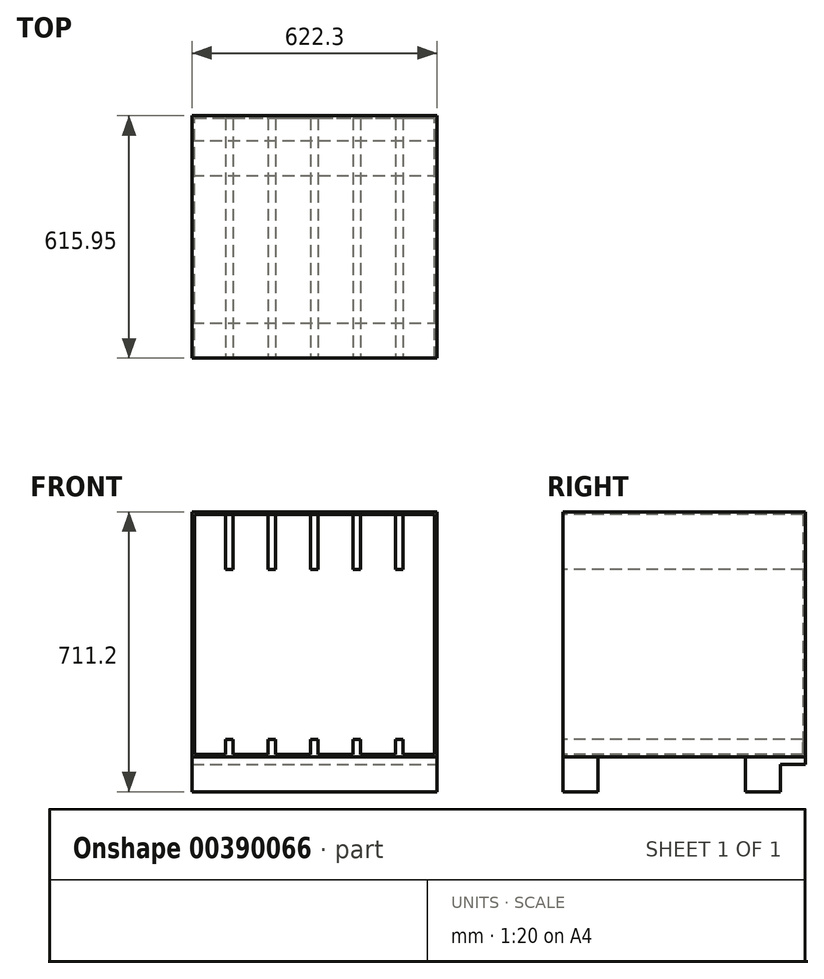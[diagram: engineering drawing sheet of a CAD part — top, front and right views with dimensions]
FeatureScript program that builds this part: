
annotation { "Feature Type Name" : "Feature", "Feature Type Description" : "" }
export const myFeature = defineFeature(function(context is Context, id is Id, definition is map)
    precondition{}
    {
        {
            var Q0;
            Q0=qCreatedBy(makeId("Front.planeOp"),FACE);
            var sketch = newSketch(context, id + "F0", { "sketchPlane" : qUnion([Q0])});
            skLineSegment(sketch, "E0.bottom", {"start": v(-311.15, 311.15) * mm, "end": v(311.15, 311.15) * mm});
            skLineSegment(sketch, "E0.top", {"start": v(-311.15, -311.15) * mm, "end": v(311.15, -311.15) * mm});
            skLineSegment(sketch, "E0.left", {"start": v(-311.15, 311.15) * mm, "end": v(-311.15, -311.15) * mm});
            skLineSegment(sketch, "E0.right", {"start": v(311.15, 311.15) * mm, "end": v(311.15, -311.15) * mm});
            skLineSegment(sketch, "E1", {"start": v(-311.15, 311.15) * mm, "end": v(311.15, -311.15) * mm, "construction": true});
            skSolve(sketch);
        }
        {
            var Q0;
            Q0 = qSketchRegion(id + "F0", true);
            extrude(context, id + "F1", {"entities" : qUnion([Q0]), "depth" : 615.95 * mm, "offsetDistance" : 25.4 * mm});
        }
        {
            var Q0;
            Q0=makeQuery(id+"F1.opExtrude","CAP_FACE",FACE,{"disambiguationData":[OSD([sQuery(id+"F0.wireOp",EDGE,"E0.bottom"),sQuery(id+"F0.wireOp",EDGE,"E0.top"),sQuery(id+"F0.wireOp",EDGE,"E0.left"),sQuery(id+"F0.wireOp",EDGE,"E0.right")])],"isStart":false});
            shell(context, id + "F2", {"entities" : qUnion([Q0]), "thickness" : 6.35 * mm});
        }
        {
            var Q0;
            Q0=makeQuery(id+"F1.opExtrude","SWEPT_FACE",FACE,{"disambiguationData":[OSD([sQuery(id+"F0.wireOp",EDGE,"E0.right")])]});
            var sketch = newSketch(context, id + "F3", { "sketchPlane" : qUnion([Q0])});
            skLineSegment(sketch, "E2.bottom", {"start": v(-615.95, -311.15) * mm, "end": v(-527.05, -311.15) * mm});
            skLineSegment(sketch, "E2.top", {"start": v(-615.95, -400.05) * mm, "end": v(-527.05, -400.05) * mm});
            skLineSegment(sketch, "E2.left", {"start": v(-615.95, -311.15) * mm, "end": v(-615.95, -400.05) * mm});
            skLineSegment(sketch, "E2.right", {"start": v(-527.05, -311.15) * mm, "end": v(-527.05, -400.05) * mm});
            skLineSegment(sketch, "E3.bottom", {"start": v(-63.5, -311.15) * mm, "end": v(-152.4, -311.15) * mm});
            skLineSegment(sketch, "E3.top", {"start": v(-63.5, -400.05) * mm, "end": v(-152.4, -400.05) * mm});
            skLineSegment(sketch, "E3.left", {"start": v(-63.5, -311.15) * mm, "end": v(-63.5, -400.05) * mm});
            skLineSegment(sketch, "E3.right", {"start": v(-152.4, -311.15) * mm, "end": v(-152.4, -400.05) * mm});
            skLineSegment(sketch, "E4.bottom", {"start": v(0, -311.15) * mm, "end": v(-63.5, -311.15) * mm});
            skLineSegment(sketch, "E4.top", {"start": v(0, -330.2) * mm, "end": v(-63.5, -330.2) * mm});
            skLineSegment(sketch, "E4.left", {"start": v(0, -311.15) * mm, "end": v(0, -330.2) * mm});
            skLineSegment(sketch, "E4.right", {"start": v(-63.5, -311.15) * mm, "end": v(-63.5, -330.2) * mm});
            skSolve(sketch);
        }
        {
            var Q0;
            Q0=makeQuery(id+"F3.imprint","IMPRINT",FACE,{"disambiguationData":[TD([[makeQuery(id+"F3.imprint","IMPRINT",EDGE,{"derivedFrom":sQuery(id+"F3.wireOp",EDGE,"E2.bottom")}),-1.0]])]});
            var Q1;
            Q1=makeQuery(id+"F3.imprint","IMPRINT",FACE,{"disambiguationData":[TD([[makeQuery(id+"F3.imprint","IMPRINT",EDGE,{"derivedFrom":sQuery(id+"F3.wireOp",EDGE,"E3.bottom")}),-1.0]])]});
            var Q2;
            Q2=makeQuery(id+"F3.imprint","IMPRINT",FACE,{"disambiguationData":[TD([[makeQuery(id+"F3.imprint","IMPRINT",EDGE,{"derivedFrom":sQuery(id+"F3.wireOp",EDGE,"E4.bottom")}),-1.0]])]});
            extrude(context, id + "F4", {"entities" : qUnion([Q0, Q1, Q2]), "oppositeDirection" : true, "depth" : 622.3 * mm, "offsetDistance" : 25.4 * mm});
        }
        {
            var Q0;
            Q0=makeQuery(id+"F1.opExtrude","CAP_FACE",FACE,{"disambiguationData":[OSD([sQuery(id+"F0.wireOp",EDGE,"E0.bottom"),sQuery(id+"F0.wireOp",EDGE,"E0.top"),sQuery(id+"F0.wireOp",EDGE,"E0.left"),sQuery(id+"F0.wireOp",EDGE,"E0.right")])],"isStart":false});
            var sketch = newSketch(context, id + "F5", { "sketchPlane" : qUnion([Q0])});
            skLineSegment(sketch, "E5.bottom", {"start": v(-225.43, -304.8) * mm, "end": v(-206.38, -304.8) * mm});
            skLineSegment(sketch, "E5.top", {"start": v(-225.43, -266.7) * mm, "end": v(-206.38, -266.7) * mm});
            skLineSegment(sketch, "E5.left", {"start": v(-225.43, -304.8) * mm, "end": v(-225.43, -266.7) * mm});
            skLineSegment(sketch, "E5.right", {"start": v(-206.38, -304.8) * mm, "end": v(-206.38, -266.7) * mm});
            skLineSegment(sketch, "E6.1.0.0", {"start": v(-117.48, -304.8) * mm, "end": v(-98.43, -304.8) * mm});
            skLineSegment(sketch, "E6.1.0.1", {"start": v(-98.43, -304.8) * mm, "end": v(-98.43, -266.7) * mm});
            skLineSegment(sketch, "E6.1.0.2", {"start": v(-117.48, -266.7) * mm, "end": v(-98.43, -266.7) * mm});
            skLineSegment(sketch, "E6.1.0.3", {"start": v(-117.48, -304.8) * mm, "end": v(-117.48, -266.7) * mm});
            skLineSegment(sketch, "E6.2.0.0", {"start": v(-9.53, -304.8) * mm, "end": v(9.52, -304.8) * mm});
            skLineSegment(sketch, "E6.2.0.1", {"start": v(9.52, -304.8) * mm, "end": v(9.52, -266.7) * mm});
            skLineSegment(sketch, "E6.2.0.2", {"start": v(-9.53, -266.7) * mm, "end": v(9.52, -266.7) * mm});
            skLineSegment(sketch, "E6.2.0.3", {"start": v(-9.53, -304.8) * mm, "end": v(-9.53, -266.7) * mm});
            skLineSegment(sketch, "E6.3.0.0", {"start": v(98.42, -304.8) * mm, "end": v(117.47, -304.8) * mm});
            skLineSegment(sketch, "E6.3.0.1", {"start": v(117.47, -304.8) * mm, "end": v(117.47, -266.7) * mm});
            skLineSegment(sketch, "E6.3.0.2", {"start": v(98.42, -266.7) * mm, "end": v(117.47, -266.7) * mm});
            skLineSegment(sketch, "E6.3.0.3", {"start": v(98.42, -304.8) * mm, "end": v(98.42, -266.7) * mm});
            skLineSegment(sketch, "E6.4.0.0", {"start": v(206.37, -304.8) * mm, "end": v(225.42, -304.8) * mm});
            skLineSegment(sketch, "E6.4.0.1", {"start": v(225.42, -304.8) * mm, "end": v(225.42, -266.7) * mm});
            skLineSegment(sketch, "E6.4.0.2", {"start": v(206.37, -266.7) * mm, "end": v(225.42, -266.7) * mm});
            skLineSegment(sketch, "E6.4.0.3", {"start": v(206.37, -304.8) * mm, "end": v(206.37, -266.7) * mm});
            skLineSegment(sketch, "E6.direction1", {"start": v(-225.43, -304.8) * mm, "end": v(-117.48, -304.8) * mm, "construction": true});
            skSolve(sketch);
        }
        {
            var Q0;
            Q0 = qSketchRegion(id + "F5", true);
            extrude(context, id + "F6", {"entities" : qUnion([Q0]), "operationType" : NewBodyOperationType.ADD, "oppositeDirection" : true, "depth" : 609.6 * mm, "offsetDistance" : 25.4 * mm});
        }
        {
            var Q0;
            Q0=makeQuery(id+"F6.boolean.opBoolean","MERGE",FACE,{"derivedFrom":[makeQuery(id+"F1.opExtrude","CAP_FACE",FACE,{"disambiguationData":[OSD([sQuery(id+"F0.wireOp",EDGE,"E0.bottom"),sQuery(id+"F0.wireOp",EDGE,"E0.top"),sQuery(id+"F0.wireOp",EDGE,"E0.left"),sQuery(id+"F0.wireOp",EDGE,"E0.right")])],"isStart":false}),makeQuery(id+"F6.opExtrude","CAP_FACE",FACE,{"disambiguationData":[OSD([sQuery(id+"F5.wireOp",EDGE,"E5.bottom"),sQuery(id+"F5.wireOp",EDGE,"E5.top"),sQuery(id+"F5.wireOp",EDGE,"E5.left"),sQuery(id+"F5.wireOp",EDGE,"E5.right")])],"isStart":true}),makeQuery(id+"F6.opExtrude","CAP_FACE",FACE,{"disambiguationData":[OSD([sQuery(id+"F5.wireOp",EDGE,"E6.1.0.0"),sQuery(id+"F5.wireOp",EDGE,"E6.1.0.1"),sQuery(id+"F5.wireOp",EDGE,"E6.1.0.2"),sQuery(id+"F5.wireOp",EDGE,"E6.1.0.3")])],"isStart":true}),makeQuery(id+"F6.opExtrude","CAP_FACE",FACE,{"disambiguationData":[OSD([sQuery(id+"F5.wireOp",EDGE,"E6.2.0.0"),sQuery(id+"F5.wireOp",EDGE,"E6.2.0.1"),sQuery(id+"F5.wireOp",EDGE,"E6.2.0.2"),sQuery(id+"F5.wireOp",EDGE,"E6.2.0.3")])],"isStart":true}),makeQuery(id+"F6.opExtrude","CAP_FACE",FACE,{"disambiguationData":[OSD([sQuery(id+"F5.wireOp",EDGE,"E6.3.0.0"),sQuery(id+"F5.wireOp",EDGE,"E6.3.0.1"),sQuery(id+"F5.wireOp",EDGE,"E6.3.0.2"),sQuery(id+"F5.wireOp",EDGE,"E6.3.0.3")])],"isStart":true}),makeQuery(id+"F6.opExtrude","CAP_FACE",FACE,{"disambiguationData":[OSD([sQuery(id+"F5.wireOp",EDGE,"E6.4.0.0"),sQuery(id+"F5.wireOp",EDGE,"E6.4.0.1"),sQuery(id+"F5.wireOp",EDGE,"E6.4.0.2"),sQuery(id+"F5.wireOp",EDGE,"E6.4.0.3")])],"isStart":true})]});
            var sketch = newSketch(context, id + "F7", { "sketchPlane" : qUnion([Q0])});
            skLineSegment(sketch, "E7.bottom", {"start": v(-225.43, 304.8) * mm, "end": v(-206.38, 304.8) * mm});
            skLineSegment(sketch, "E7.top", {"start": v(-225.43, 165.1) * mm, "end": v(-206.38, 165.1) * mm});
            skLineSegment(sketch, "E7.left", {"start": v(-225.43, 304.8) * mm, "end": v(-225.43, 165.1) * mm});
            skLineSegment(sketch, "E7.right", {"start": v(-206.38, 304.8) * mm, "end": v(-206.38, 165.1) * mm});
            skLineSegment(sketch, "E8.1.0.0", {"start": v(-117.48, 304.8) * mm, "end": v(-117.48, 165.1) * mm});
            skLineSegment(sketch, "E8.1.0.1", {"start": v(-117.48, 304.8) * mm, "end": v(-98.43, 304.8) * mm});
            skLineSegment(sketch, "E8.1.0.2", {"start": v(-98.43, 304.8) * mm, "end": v(-98.43, 165.1) * mm});
            skLineSegment(sketch, "E8.1.0.3", {"start": v(-117.48, 165.1) * mm, "end": v(-98.43, 165.1) * mm});
            skLineSegment(sketch, "E8.2.0.0", {"start": v(-9.53, 304.8) * mm, "end": v(-9.53, 165.1) * mm});
            skLineSegment(sketch, "E8.2.0.1", {"start": v(-9.53, 304.8) * mm, "end": v(9.52, 304.8) * mm});
            skLineSegment(sketch, "E8.2.0.2", {"start": v(9.52, 304.8) * mm, "end": v(9.52, 165.1) * mm});
            skLineSegment(sketch, "E8.2.0.3", {"start": v(-9.53, 165.1) * mm, "end": v(9.52, 165.1) * mm});
            skLineSegment(sketch, "E8.3.0.0", {"start": v(98.42, 304.8) * mm, "end": v(98.42, 165.1) * mm});
            skLineSegment(sketch, "E8.3.0.1", {"start": v(98.42, 304.8) * mm, "end": v(117.47, 304.8) * mm});
            skLineSegment(sketch, "E8.3.0.2", {"start": v(117.47, 304.8) * mm, "end": v(117.47, 165.1) * mm});
            skLineSegment(sketch, "E8.3.0.3", {"start": v(98.42, 165.1) * mm, "end": v(117.47, 165.1) * mm});
            skLineSegment(sketch, "E8.4.0.0", {"start": v(206.37, 304.8) * mm, "end": v(206.37, 165.1) * mm});
            skLineSegment(sketch, "E8.4.0.1", {"start": v(206.37, 304.8) * mm, "end": v(225.42, 304.8) * mm});
            skLineSegment(sketch, "E8.4.0.2", {"start": v(225.42, 304.8) * mm, "end": v(225.42, 165.1) * mm});
            skLineSegment(sketch, "E8.4.0.3", {"start": v(206.37, 165.1) * mm, "end": v(225.42, 165.1) * mm});
            skLineSegment(sketch, "E8.direction1", {"start": v(-225.43, 165.1) * mm, "end": v(-117.48, 165.1) * mm, "construction": true});
            skSolve(sketch);
        }
        {
            var Q0;
            Q0 = qSketchRegion(id + "F7", true);
            extrude(context, id + "F8", {"entities" : qUnion([Q0]), "oppositeDirection" : true, "depth" : 609.6 * mm, "offsetDistance" : 25.4 * mm});
        }
    });
